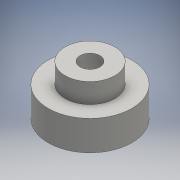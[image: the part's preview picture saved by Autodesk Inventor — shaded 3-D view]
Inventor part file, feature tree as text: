
AUTODESK INVENTOR PART (.ipt)
format: ipt  version: 2016 SP1 (Build 200210100, 210)  size: 103,424 bytes
history: native  units: mm
features: extrude x2, sketch x2
ambient origin geometry x8: Origin, YZ Plane, XZ Plane, XY Plane, X Axis, Y Axis, Z Axis, Center Point
bodies: Solid1 (feature_tree)
feature tree (4):
  extrude  "Extrusion1"  Depth=10.0mm
  extrude  "Extrusion2"  Depth=25.0mm
  sketch  "Sketch1"  dims[d0=10.0mm d1=42.0mm]
  sketch  "Sketch2"  dims[d2=15.0mm d3=0.0mm d4=25.0mm d5=10.0mm d6=0.0mm]
